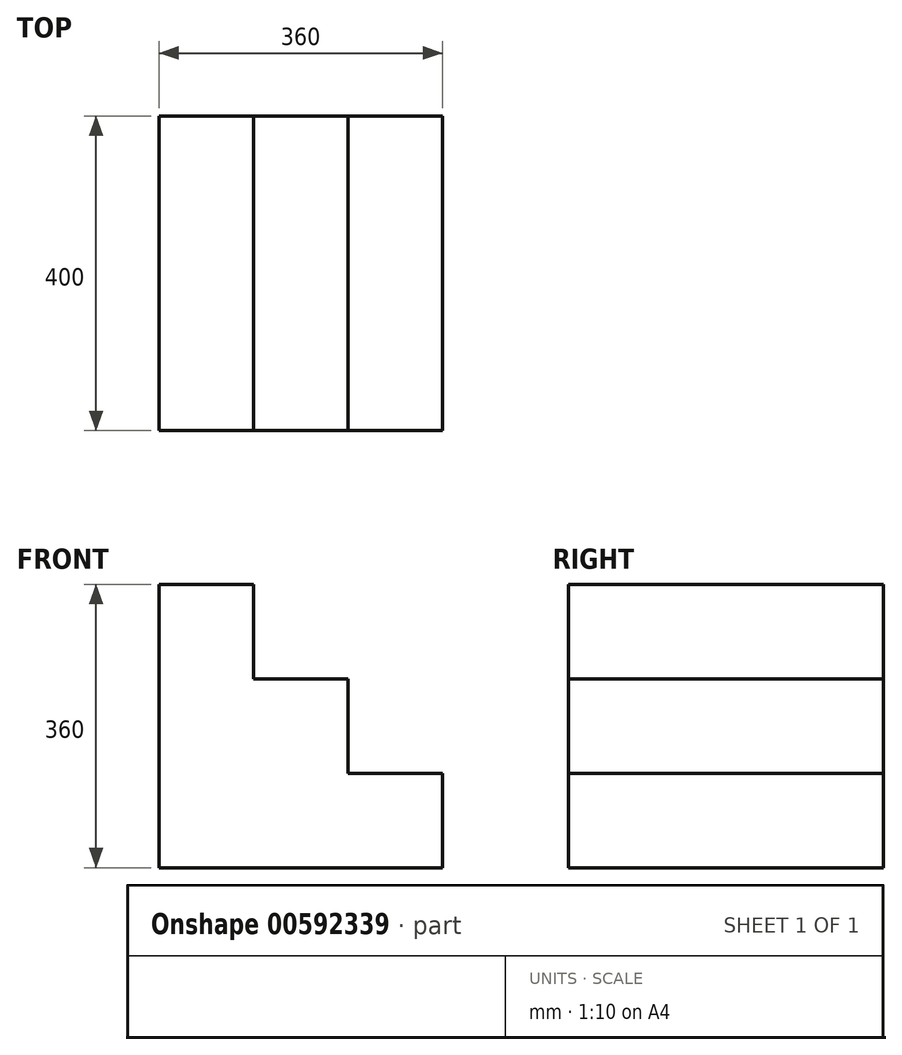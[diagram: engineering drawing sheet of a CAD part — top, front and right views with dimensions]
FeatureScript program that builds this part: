
annotation { "Feature Type Name" : "Feature", "Feature Type Description" : "" }
export const myFeature = defineFeature(function(context is Context, id is Id, definition is map)
    precondition{}
    {
        {
            var Q0;
            Q0=qCreatedBy(makeId("Front.planeOp"),FACE);
            var sketch = newSketch(context, id + "F0", { "sketchPlane" : qUnion([Q0])});
            skLineSegment(sketch, "E0", {"start": v(0, 0) * mm, "end": v(0, 360) * mm});
            skLineSegment(sketch, "E1", {"start": v(0, 0) * mm, "end": v(360, 0) * mm});
            skLineSegment(sketch, "E2", {"start": v(0, 360) * mm, "end": v(120, 360) * mm});
            skLineSegment(sketch, "E3", {"start": v(120, 360) * mm, "end": v(120, 240) * mm});
            skLineSegment(sketch, "E4", {"start": v(120, 240) * mm, "end": v(240, 240) * mm});
            skLineSegment(sketch, "E5", {"start": v(240, 240) * mm, "end": v(240, 120) * mm});
            skLineSegment(sketch, "E6", {"start": v(240, 120) * mm, "end": v(360, 120) * mm});
            skPoint(sketch, "E7.start.orphan", {"position": v(360, 120) * mm});
            skLineSegment(sketch, "E8", {"start": v(360, 120) * mm, "end": v(360, 0) * mm});
            skSolve(sketch);
        }
        {
            var Q0;
            Q0 = qSketchRegion(id + "F0", true);
            extrude(context, id + "F1", {"entities" : qUnion([Q0]), "depth" : 400 * mm, "offsetDistance" : 25 * mm});
        }
    });
